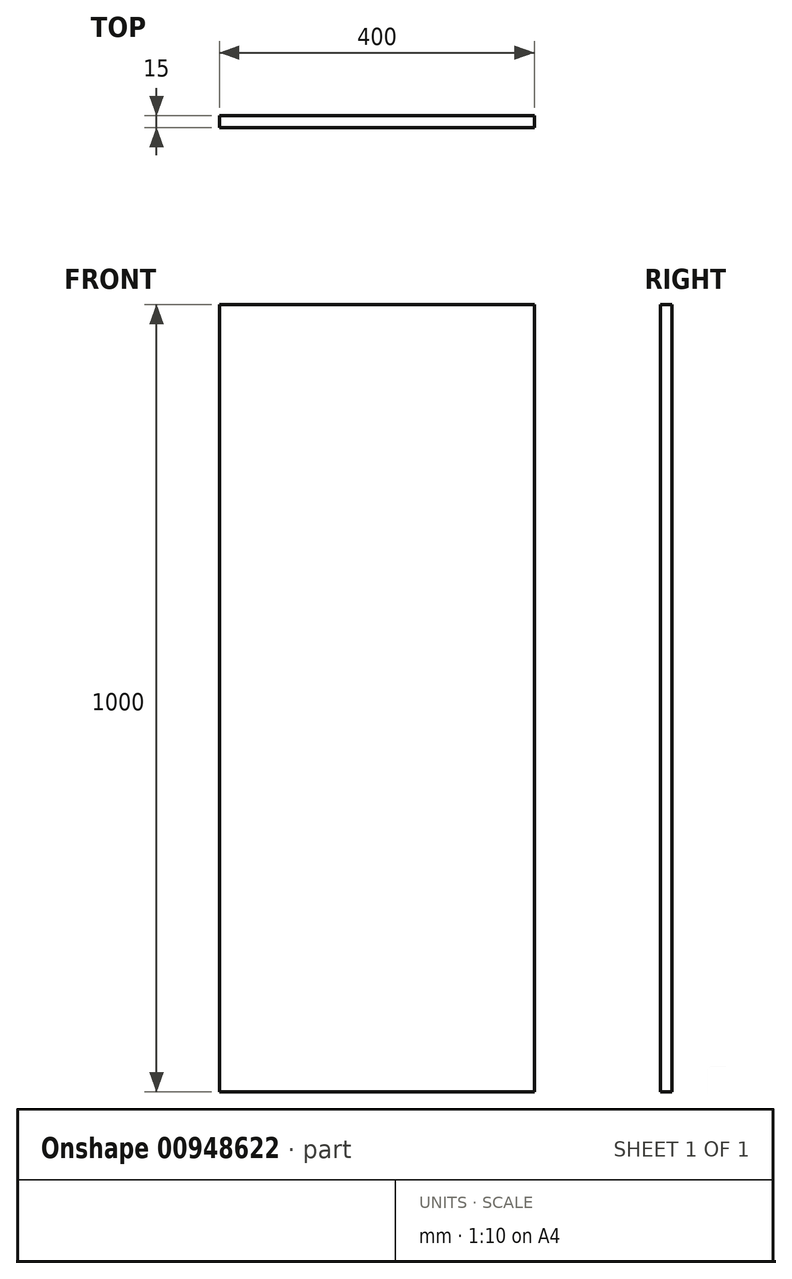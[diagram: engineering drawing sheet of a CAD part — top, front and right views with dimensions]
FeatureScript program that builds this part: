
annotation { "Feature Type Name" : "Feature", "Feature Type Description" : "" }
export const myFeature = defineFeature(function(context is Context, id is Id, definition is map)
    precondition{}
    {
        {
            var Q0;
            Q0=qCreatedBy(makeId("Front.planeOp"),FACE);
            var sketch = newSketch(context, id + "F0", { "sketchPlane" : qUnion([Q0])});
            skLineSegment(sketch, "E0.bottom", {"start": v(0, 0) * mm, "end": v(400, 0) * mm});
            skLineSegment(sketch, "E0.top", {"start": v(0, 1000) * mm, "end": v(400, 1000) * mm});
            skLineSegment(sketch, "E0.left", {"start": v(0, 0) * mm, "end": v(0, 1000) * mm});
            skLineSegment(sketch, "E0.right", {"start": v(400, 0) * mm, "end": v(400, 1000) * mm});
            skSolve(sketch);
        }
        {
            var Q0;
            Q0 = qSketchRegion(id + "F0", true);
            extrude(context, id + "F1", {"entities" : qUnion([Q0]), "depth" : 15 * mm, "offsetDistance" : 25 * mm});
        }
    });
